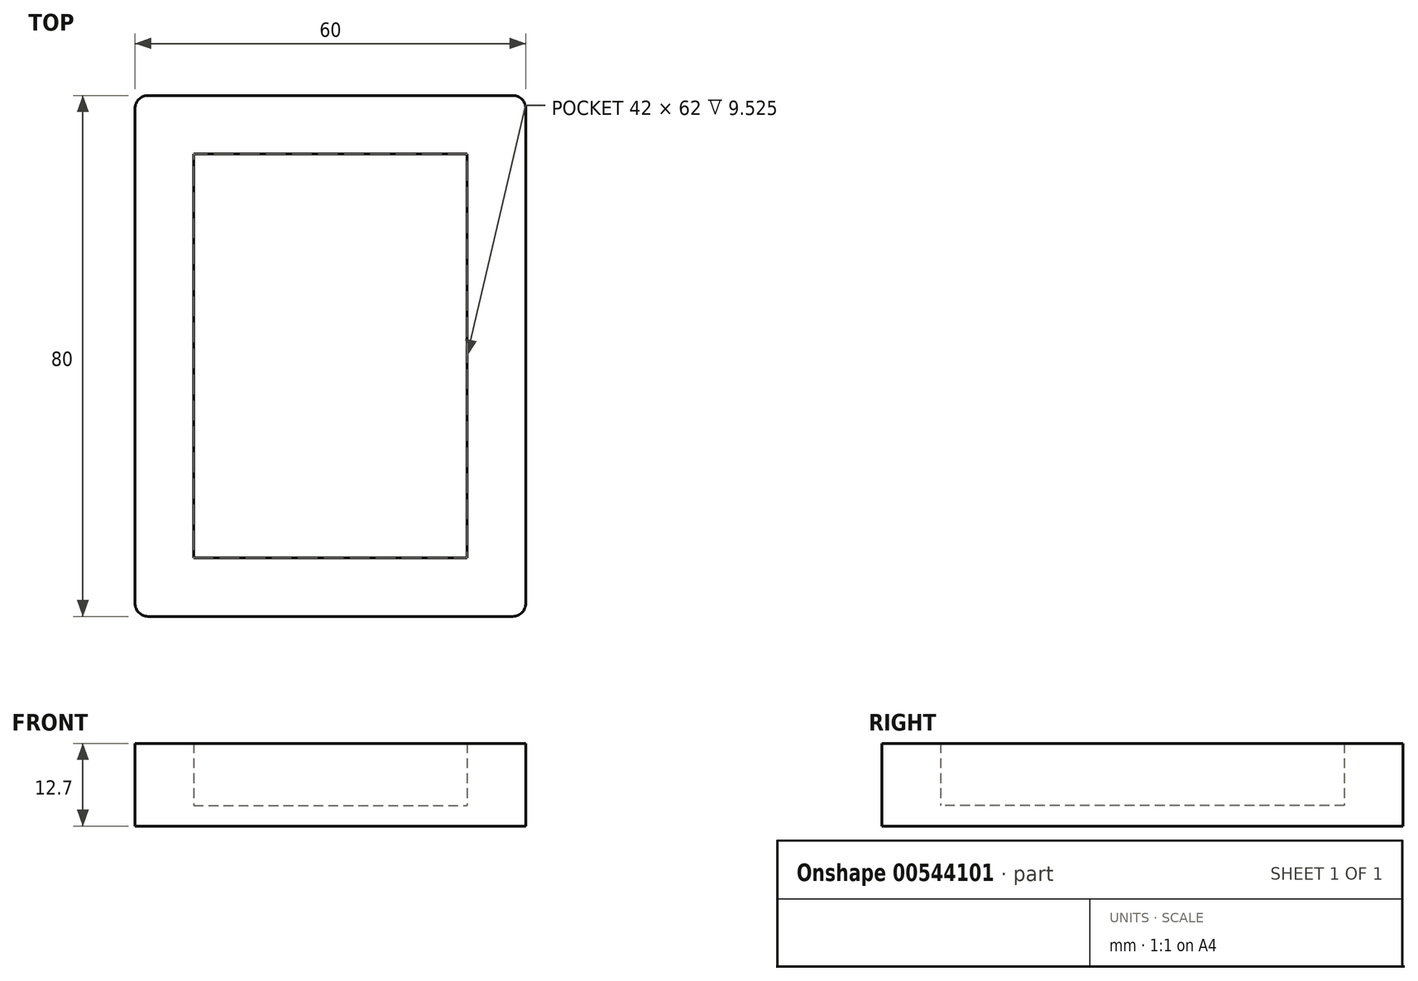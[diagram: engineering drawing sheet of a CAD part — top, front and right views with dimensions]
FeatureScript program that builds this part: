
annotation { "Feature Type Name" : "Feature", "Feature Type Description" : "" }
export const myFeature = defineFeature(function(context is Context, id is Id, definition is map)
    precondition{}
    {
        {
            var Q0;
            Q0=qCreatedBy(makeId("Top.planeOp"),FACE);
            var sketch = newSketch(context, id + "F0", { "sketchPlane" : qUnion([Q0])});
            skLineSegment(sketch, "E0.bottom", {"start": v(10, 70) * mm, "end": v(50, 70) * mm});
            skLineSegment(sketch, "E0.top", {"start": v(10, 10) * mm, "end": v(50, 10) * mm});
            skLineSegment(sketch, "E0.left", {"start": v(10, 70) * mm, "end": v(10, 10) * mm});
            skLineSegment(sketch, "E0.right", {"start": v(50, 70) * mm, "end": v(50, 10) * mm});
            skLineSegment(sketch, "E1.bottom", {"start": v(2, 0) * mm, "end": v(58, 0) * mm});
            skLineSegment(sketch, "E1.top", {"start": v(2, 80) * mm, "end": v(58, 80) * mm});
            skLineSegment(sketch, "E1.left", {"start": v(0, 2) * mm, "end": v(0, 78) * mm});
            skLineSegment(sketch, "E1.right", {"start": v(60, 2) * mm, "end": v(60, 78) * mm});
            skLineSegment(sketch, "E2.0", {"start": v(51, 71) * mm, "end": v(51, 9) * mm});
            skLineSegment(sketch, "E2.1", {"start": v(9, 71) * mm, "end": v(51, 71) * mm});
            skLineSegment(sketch, "E2.2", {"start": v(9, 71) * mm, "end": v(9, 9) * mm});
            skLineSegment(sketch, "E2.3", {"start": v(9, 9) * mm, "end": v(51, 9) * mm});
            skLineSegment(sketch, "E3", {"start": v(9, 71) * mm, "end": v(9, 80) * mm});
            skLineSegment(sketch, "E4", {"start": v(51, 9) * mm, "end": v(51, 0) * mm});
            skLineSegment(sketch, "E5", {"start": v(51, 71) * mm, "end": v(60, 71) * mm});
            skLineSegment(sketch, "E6", {"start": v(9, 9) * mm, "end": v(0, 9) * mm});
            skPoint(sketch, "E7.visualSharp", {"position": v(0, 80) * mm});
            skArc(sketch, "E7.filletArc", {"start": v(2, 80) * mm, "mid": v(0.59, 79.41) * mm, "end": v(0, 78) * mm});
            skPoint(sketch, "E8.visualSharp", {"position": v(60, 80) * mm});
            skArc(sketch, "E8.filletArc", {"start": v(60, 78) * mm, "mid": v(59.41, 79.41) * mm, "end": v(58, 80) * mm});
            skPoint(sketch, "E9.visualSharp", {"position": v(60, 0) * mm});
            skArc(sketch, "E9.filletArc", {"start": v(58, 0) * mm, "mid": v(59.41, 0.59) * mm, "end": v(60, 2) * mm});
            skPoint(sketch, "E10.visualSharp", {"position": v(0, 0) * mm});
            skArc(sketch, "E10.filletArc", {"start": v(0, 2) * mm, "mid": v(0.59, 0.59) * mm, "end": v(2, 0) * mm});
            skSolve(sketch);
        }
        {
            var Q0;
            Q0=makeQuery(id+"F0.imprint","IMPRINT",FACE,{"disambiguationData":[TD([[makeQuery(id+"F0.imprint","IMPRINT",EDGE,{"derivedFrom":sQuery(id+"F0.wireOp",EDGE,"E2.2")}),-1.0]])]});
            var Q1;
            Q1=makeQuery(id+"F0.imprint","IMPRINT",FACE,{"disambiguationData":[TD([[makeQuery(id+"F0.imprint","IMPRINT",EDGE,{"derivedFrom":sQuery(id+"F0.wireOp",EDGE,"E2.1")}),1.0]])]});
            var Q2;
            Q2=makeQuery(id+"F0.imprint","IMPRINT",FACE,{"disambiguationData":[TD([[makeQuery(id+"F0.imprint","IMPRINT",EDGE,{"derivedFrom":sQuery(id+"F0.wireOp",EDGE,"E2.0")}),1.0]])]});
            var Q3;
            Q3=makeQuery(id+"F0.imprint","IMPRINT",FACE,{"disambiguationData":[TD([[makeQuery(id+"F0.imprint","IMPRINT",EDGE,{"derivedFrom":sQuery(id+"F0.wireOp",EDGE,"E2.3")}),-1.0]])]});
            extrude(context, id + "F1", {"entities" : qUnion([Q0, Q1, Q2, Q3]), "depth" : 12.7 * mm, "offsetDistance" : 25 * mm});
        }
        {
            var Q0;
            Q0=makeQuery(id+"F0.imprint","IMPRINT",FACE,{"disambiguationData":[TD([[makeQuery(id+"F0.imprint","IMPRINT",EDGE,{"derivedFrom":sQuery(id+"F0.wireOp",EDGE,"E0.bottom")}),1.0]])]});
            var Q1;
            Q1=makeQuery(id+"F0.imprint","IMPRINT",FACE,{"disambiguationData":[TD([[makeQuery(id+"F0.imprint","IMPRINT",EDGE,{"derivedFrom":sQuery(id+"F0.wireOp",EDGE,"E0.bottom")}),-1.0]])]});
            extrude(context, id + "F2", {"entities" : qUnion([Q0, Q1]), "operationType" : NewBodyOperationType.ADD, "depth" : 3.17 * mm, "offsetDistance" : 25 * mm});
        }
    });
